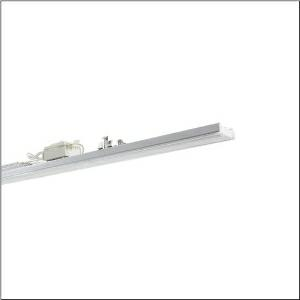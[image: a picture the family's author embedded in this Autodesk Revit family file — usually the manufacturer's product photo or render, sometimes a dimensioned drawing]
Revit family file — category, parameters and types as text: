
# Revit family: licross_r__21_recessed_mo_52te19cn485g_8aa0
name_source: partatom
category: Lighting Fixtures
units: mm (PartAtom-declared; Revit-internal decimal feet)

## family parameters
Cut with Voids When Loaded = No
Host = Face
Light Source = No
Part Type = Normal
Room Calculation Point = No
Round Connector Dimension = Use Diameter
Shared = No

## types (1)
- --- (1 x LED, 8870 lm, 49.9 W, 4000K)
    Apparent Load = 50 VA
    CIE Flux Codes = 55 90 98 100 100
    Color Rendering = 80
    Color Temperature = 4000K
    Default Elevation = 1800 mm
    Description = Licross® 21 Recessed MO, luminaire insert, of sheet steel, galvanised, coil coated, white, length: 1.500mm, width: 66mm, height: 67mm, LED rated luminous flux: 8.880lm, light colour: 840, control gear: ON/OFF Multilumen, CLOi, control gear: ECG DALI, with plug, 5-pole, with phase selection, mains connection: 220..240V, AC, 50/60Hz, start of lifetime: 50W, end of service life: 61W, internal wiring halogen-free, primary light control with lens, of plastic, primary optical cover: cover, of PMMA, light emission: direct distribution, primary light characteristic: double asymmetric, protection rating (complete): IP54, insulation class (complete): insulation class I (protective earthing), certification: CE, ENEC, VDE, UKCA, protection symbol: D if used in an environment with non-conductive dust loads with corresponding accessories, impact resistance: IK06, permissible ambient temperature for indoor applications: -35..+40°C, corresponds to IFS (International Featured Standards) requirements for safety and quality in the food industry, reducing of maximum allowable ambient temperature of 5°C with ceiling mounting, LABS conformity tested according to VDMA 24364:2018-05, packaging unit: 1 piece
    Height = 58 mm
    Lamp = 1 x LED
    Lamp Light Flux = 8870 lm
    Lamp Power = 49.9 W
    Lamp count = 1
    Length = 1500 mm
    Luminous efficacy = 178 lm/W
    Manufacturer = Siteco
    ModVariant = No
    Model = 52TE19CN485G
    Mounting Place = Ceiling
    Mounting Type = Pendant
    Number of Poles = 1
    OnlyDefault = Yes
    Power Factor = 1
    Product Name = Licross® 21 Recessed MO
    Product group = luminaire insert | ceiling pendant
    ProductGroupID = 902
    Protection Class = Protection class I
    Protection Degree = IP 54
    RLX_Detail_Level = 1
    RLX_Emergency_Light_Flux = 0 lm
    RLX_Emergency_Type = 0
    RLX_Emergency_Type_DB = No
    RlxData = <blob elided: 22349 chars, md5=bd8fab5a>
    Socket = socket
    Standby Power = 0 W
    System Light Flux = 8870 lm
    System Power = 50 W
    Type Comments = factory setting: luminous flux: 100 % | (A | C | E) | 116 mA
    Type Image = l_1296930.jpg
    URL = http://relux.com
    VarID = @adj_132275
    Voltage = 0 V
    Weight = 0.00 kg
    Width = 66 mm

## geometry (parser evidence)
native form markers: Blend x4, Sweep x11
no freeform markers — native parametric forms only
